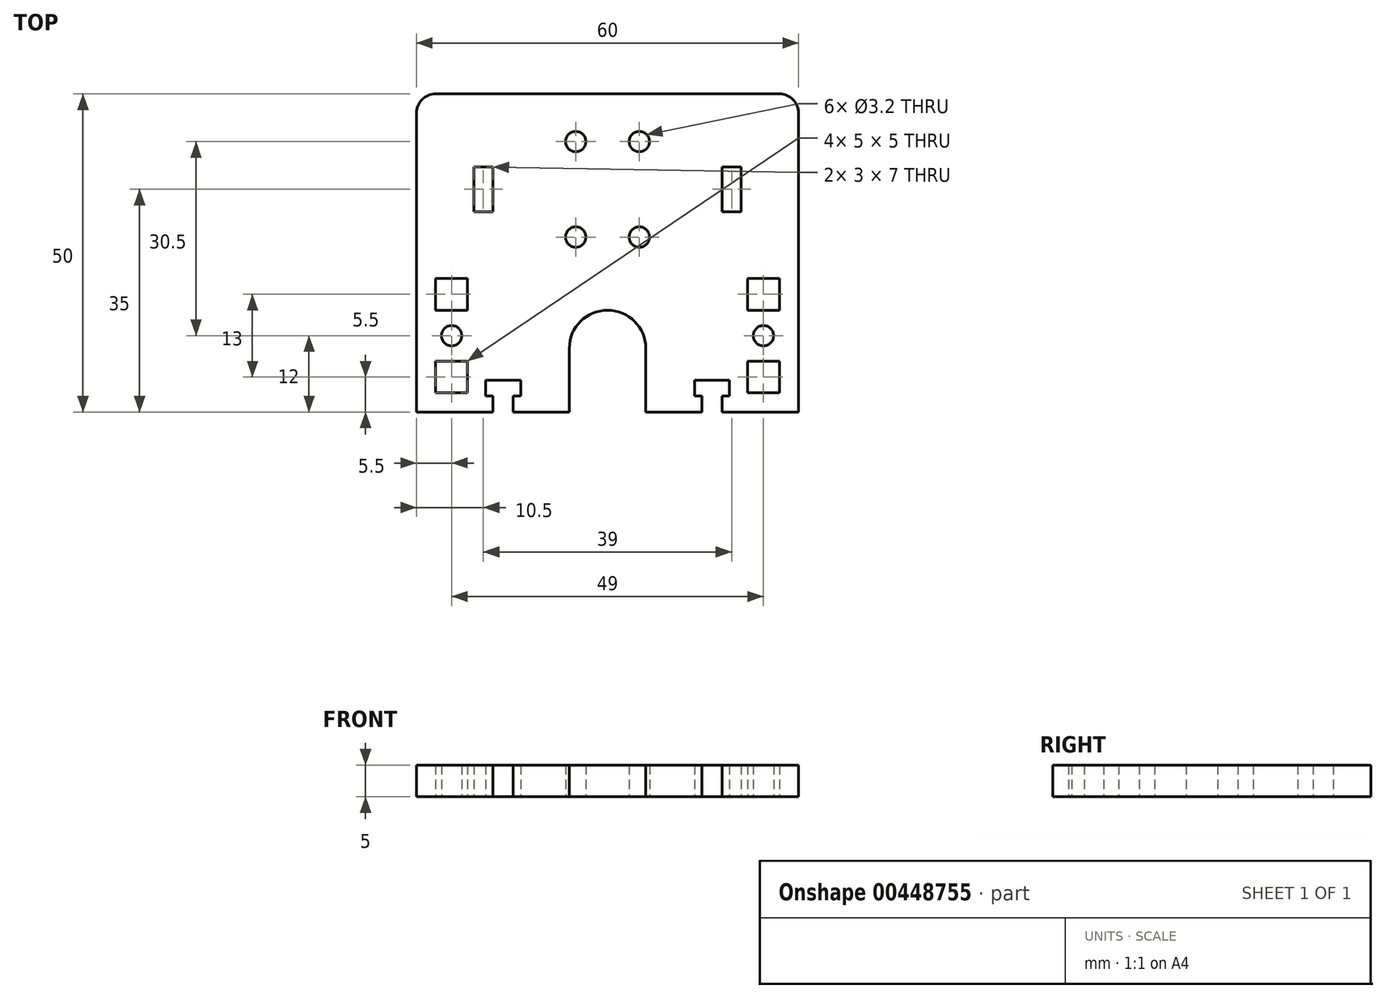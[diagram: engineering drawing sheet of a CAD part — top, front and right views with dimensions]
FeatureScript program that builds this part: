
annotation { "Feature Type Name" : "Feature", "Feature Type Description" : "" }
export const myFeature = defineFeature(function(context is Context, id is Id, definition is map)
    precondition{}
    {
        {
            assignVariable(context, id + "F0", {"name" : "thickness", "anyValue" : 5 * mm});
        }
        {
            var Q0;
            Q0=qCreatedBy(makeId("Top.planeOp"),FACE);
            var sketch = newSketch(context, id + "F1", { "sketchPlane" : qUnion([Q0])});
            skLineSegment(sketch, "E0.bottom", {"start": v(15, 10) * mm, "end": v(-15, 10) * mm, "construction": true});
            skLineSegment(sketch, "E0.top", {"start": v(15, -10) * mm, "end": v(-15, -10) * mm, "construction": true});
            skLineSegment(sketch, "E0.left", {"start": v(15, 10) * mm, "end": v(15, -10) * mm, "construction": true});
            skLineSegment(sketch, "E0.right", {"start": v(-15, 10) * mm, "end": v(-15, -10) * mm, "construction": true});
            skPoint(sketch, "E0.middle", {"position": v(0, 0) * mm});
            skLineSegment(sketch, "E1", {"start": v(-15, 0) * mm, "end": v(15, 0) * mm, "construction": true});
            skLineSegment(sketch, "E2", {"start": v(0, 10) * mm, "end": v(0, -10) * mm, "construction": true});
            skCircle(sketch, "E3", {"center": v(-5, -7.5) * mm, "radius": 1.6 * mm});
            skCircle(sketch, "E4", {"center": v(5, -7.5) * mm, "radius": 1.6 * mm});
            skCircle(sketch, "E5", {"center": v(5, 7.5) * mm, "radius": 1.6 * mm});
            skCircle(sketch, "E6", {"center": v(-5, 7.5) * mm, "radius": 1.6 * mm});
            skLineSegment(sketch, "E7", {"start": v(-5, 7.5) * mm, "end": v(5, 7.5) * mm, "construction": true});
            skLineSegment(sketch, "E8", {"start": v(5, -7.5) * mm, "end": v(5, 7.5) * mm, "construction": true});
            skPoint(sketch, "E9", {"position": v(5, 0) * mm});
            skPoint(sketch, "E10", {"position": v(0, 7.5) * mm});
            skLineSegment(sketch, "E11.top", {"start": v(27, 15) * mm, "end": v(-27, 15) * mm});
            skArc(sketch, "E12", {"start": v(6, -25) * mm, "mid": v(0, -19) * mm, "end": v(-6, -25) * mm});
            skArc(sketch, "E13", {"start": v(6, -25) * mm, "mid": v(0, -31) * mm, "end": v(-6, -25) * mm, "construction": true});
            skLineSegment(sketch, "E14", {"start": v(-6, -25) * mm, "end": v(-6, -35) * mm});
            skLineSegment(sketch, "E15", {"start": v(-6, -35) * mm, "end": v(-14.8, -35) * mm});
            skPoint(sketch, "E16.visualSharp", {"position": v(-6, -35) * mm});
            skLineSegment(sketch, "E17", {"start": v(-30, 12) * mm, "end": v(-30, -35) * mm});
            skLineSegment(sketch, "E18", {"start": v(30, 12) * mm, "end": v(30, -35) * mm});
            skLineSegment(sketch, "E19", {"start": v(30, -35) * mm, "end": v(18, -35) * mm});
            skPoint(sketch, "E20.visualSharp", {"position": v(6, -35) * mm});
            skLineSegment(sketch, "E21.bottom", {"start": v(-21, 3.5) * mm, "end": v(-18, 3.5) * mm});
            skLineSegment(sketch, "E21.top", {"start": v(-21, -3.5) * mm, "end": v(-18, -3.5) * mm});
            skLineSegment(sketch, "E21.left", {"start": v(-21, 3.5) * mm, "end": v(-21, -3.5) * mm});
            skLineSegment(sketch, "E21.right", {"start": v(-18, 3.5) * mm, "end": v(-18, -3.5) * mm});
            skPoint(sketch, "E22", {"position": v(-18, 0) * mm});
            skLineSegment(sketch, "E23.MirrorCS", {"start": v(21, 3.5) * mm, "end": v(18, 3.5) * mm});
            skLineSegment(sketch, "E24.MirrorCS", {"start": v(21, 3.5) * mm, "end": v(21, -3.5) * mm});
            skLineSegment(sketch, "E25.MirrorCS", {"start": v(21, -3.5) * mm, "end": v(18, -3.5) * mm});
            skLineSegment(sketch, "E26.MirrorCS", {"start": v(18, 3.5) * mm, "end": v(18, -3.5) * mm});
            skPoint(sketch, "E27.MirrorP", {"position": v(18, 0) * mm});
            skLineSegment(sketch, "E28.bottom", {"start": v(-27, -32) * mm, "end": v(-22, -32) * mm});
            skLineSegment(sketch, "E28.top", {"start": v(-27, -27) * mm, "end": v(-22, -27) * mm});
            skLineSegment(sketch, "E28.left", {"start": v(-27, -32) * mm, "end": v(-27, -27) * mm});
            skLineSegment(sketch, "E28.right", {"start": v(-22, -32) * mm, "end": v(-22, -27) * mm});
            skPoint(sketch, "E29.firstSnap0", {"position": v(-27, -29.5) * mm});
            skLineSegment(sketch, "E29.bottom", {"start": v(-27, -19) * mm, "end": v(-22, -19) * mm});
            skLineSegment(sketch, "E29.top", {"start": v(-27, -14) * mm, "end": v(-22, -14) * mm});
            skLineSegment(sketch, "E29.left", {"start": v(-27, -19) * mm, "end": v(-27, -14) * mm});
            skLineSegment(sketch, "E29.right", {"start": v(-22, -19) * mm, "end": v(-22, -14) * mm});
            skCircle(sketch, "E30", {"center": v(-24.5, -23) * mm, "radius": 1.6 * mm});
            skPoint(sketch, "E30.centerSnap0", {"position": v(-24.5, -19) * mm});
            skLineSegment(sketch, "E31.MirrorCS", {"start": v(22, -32) * mm, "end": v(22, -27) * mm});
            skLineSegment(sketch, "E32.MirrorCS", {"start": v(27, -32) * mm, "end": v(22, -32) * mm});
            skLineSegment(sketch, "E33.MirrorCS", {"start": v(22, -19) * mm, "end": v(22, -14) * mm});
            skLineSegment(sketch, "E34.MirrorCS", {"start": v(27, -19) * mm, "end": v(22, -19) * mm});
            skPoint(sketch, "E35.MirrorP", {"position": v(27, -29.5) * mm});
            skLineSegment(sketch, "E36.MirrorCS", {"start": v(27, -32) * mm, "end": v(27, -27) * mm});
            skPoint(sketch, "E37.MirrorP", {"position": v(24.5, -19) * mm});
            skLineSegment(sketch, "E38.MirrorCS", {"start": v(27, -14) * mm, "end": v(22, -14) * mm});
            skLineSegment(sketch, "E39.MirrorCS", {"start": v(27, -19) * mm, "end": v(27, -14) * mm});
            skLineSegment(sketch, "E40.MirrorCS", {"start": v(27, -27) * mm, "end": v(22, -27) * mm});
            skCircle(sketch, "E41.MirrorC", {"center": v(24.5, -23) * mm, "radius": 1.6 * mm});
            skPoint(sketch, "E42.visualSharp", {"position": v(-30, -35) * mm});
            skPoint(sketch, "E43.visualSharp", {"position": v(30, -35) * mm});
            skPoint(sketch, "E44.visualSharp", {"position": v(30, 15) * mm});
            skArc(sketch, "E44.filletArc", {"start": v(30, 12) * mm, "mid": v(29.12, 14.12) * mm, "end": v(27, 15) * mm});
            skPoint(sketch, "E45.visualSharp", {"position": v(-30, 15) * mm});
            skArc(sketch, "E45.filletArc", {"start": v(-27, 15) * mm, "mid": v(-29.12, 14.12) * mm, "end": v(-30, 12) * mm});
            skLineSegment(sketch, "E46.trimOffspring", {"start": v(6, -35) * mm, "end": v(6, -25) * mm});
            skLineSegment(sketch, "E47", {"start": v(-18, -35) * mm, "end": v(-18, -32.5) * mm});
            skLineSegment(sketch, "E48", {"start": v(-18, -32.5) * mm, "end": v(-19.15, -32.5) * mm});
            skLineSegment(sketch, "E49", {"start": v(-19.15, -32.5) * mm, "end": v(-19.15, -30) * mm});
            skLineSegment(sketch, "E50", {"start": v(-19.15, -30) * mm, "end": v(-16.4, -30) * mm});
            skLineSegment(sketch, "E51", {"start": v(-16.4, -30) * mm, "end": v(-16.4, -35) * mm, "construction": true});
            skLineSegment(sketch, "E52.MirrorCS", {"start": v(-13.65, -30) * mm, "end": v(-16.4, -30) * mm});
            skLineSegment(sketch, "E53.MirrorCS", {"start": v(-13.65, -32.5) * mm, "end": v(-13.65, -30) * mm});
            skLineSegment(sketch, "E54.MirrorCS", {"start": v(-14.8, -32.5) * mm, "end": v(-13.65, -32.5) * mm});
            skLineSegment(sketch, "E55.MirrorCS", {"start": v(-14.8, -35) * mm, "end": v(-14.8, -32.5) * mm});
            skLineSegment(sketch, "E56.MirrorCS", {"start": v(14.8, -32.5) * mm, "end": v(13.65, -32.5) * mm});
            skLineSegment(sketch, "E57.MirrorCS", {"start": v(18, -32.5) * mm, "end": v(19.15, -32.5) * mm});
            skLineSegment(sketch, "E58.MirrorCS", {"start": v(14.8, -35) * mm, "end": v(14.8, -32.5) * mm});
            skLineSegment(sketch, "E59.MirrorCS", {"start": v(19.15, -32.5) * mm, "end": v(19.15, -30) * mm});
            skLineSegment(sketch, "E60.MirrorCS", {"start": v(19.15, -30) * mm, "end": v(16.4, -30) * mm});
            skLineSegment(sketch, "E61.MirrorCS", {"start": v(18, -35) * mm, "end": v(18, -32.5) * mm});
            skLineSegment(sketch, "E62.MirrorCS", {"start": v(13.65, -30) * mm, "end": v(16.4, -30) * mm});
            skLineSegment(sketch, "E63.MirrorCS", {"start": v(16.4, -30) * mm, "end": v(16.4, -35) * mm, "construction": true});
            skLineSegment(sketch, "E64.MirrorCS", {"start": v(13.65, -32.5) * mm, "end": v(13.65, -30) * mm});
            skLineSegment(sketch, "E65.trimOffspring", {"start": v(-18, -35) * mm, "end": v(-30, -35) * mm});
            skLineSegment(sketch, "E66.trimOffspring", {"start": v(14.8, -35) * mm, "end": v(6, -35) * mm});
            skSolve(sketch);
        }
        {
            var Q0;
            Q0=qSketchRegion(id+"F1",true);
            extrude(context, id + "F2", {"entities" : qUnion([Q0]), "depth" : getVariable(context, 'thickness')});
        }
    });
